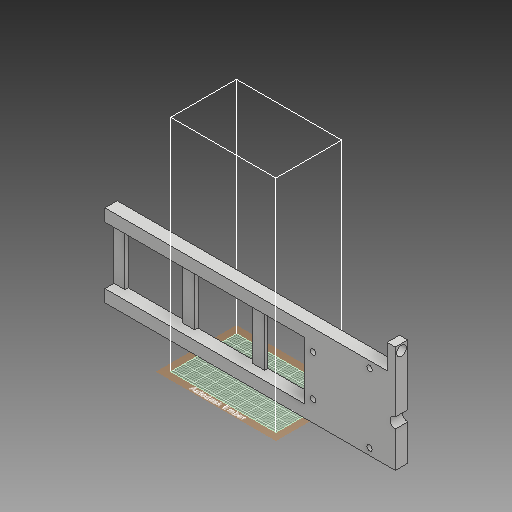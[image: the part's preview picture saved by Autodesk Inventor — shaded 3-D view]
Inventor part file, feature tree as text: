
AUTODESK INVENTOR PART (.ipt)
format: ipt  version: 2018 (Build 220112000, 112)  size: 1,129,472 bytes
history: native  units: mm
features: sketch x81, extrude x64, fillet x22, hole x8
ambient origin geometry x8: Origin, YZ Plane, XZ Plane, XY Plane, X Axis, Y Axis, Z Axis, Center Point
bodies: Solid1 (feature_tree)
feature tree (175):
  extrude  "Extrusion1"  Depth=50.0mm
  hole  "Hole1"  [1 undecoded]
  hole  "Hole2"  [1 undecoded]
  extrude  "Extrusion2"  Depth=25.0mm
  extrude  "Extrusion3"  Depth=25.0mm
  extrude  "Extrusion4"  Depth=5.0mm
  sketch  "Sketch7"  dims[d25=10.0mm d26=5.0mm]
  extrude  "Extrusion5"  Depth=5.0mm
  extrude  "Extrusion6"  Depth=35.0mm
  extrude  "Extrusion7"  Depth=35.0mm
  extrude  "Extrusion8"  Depth=35.0mm
  extrude  "Extrusion9"  Depth=2.0mm TaperAngle=0.0deg
  extrude  "Extrusion10"  Depth=7.5mm TaperAngle=0.0deg
  extrude  "Extrusion11"  Depth=10.0mm
  extrude  "Extrusion12"  Depth=7.5mm
  fillet  "Fillet1"  Radius=7.5mm
  fillet  "Fillet2"  Radius=25.0mm
  fillet  "Fillet3"  Radius=3.0mm
  fillet  "Fillet4"  Radius=3.2mm
  fillet  "Fillet5"  Radius=2.1mm
  fillet  "Fillet6"  Radius=5.5mm
  extrude  "Extrusion13"  Depth=92.5mm TaperAngle=0.0deg
  sketch  "Sketch17"  dims[d58=4.25mm d59=241.0mm d60=0.0mm]
  hole  "Hole3"  [1 undecoded]
  hole  "Hole4"  [1 undecoded]
  extrude  "Extrusion14"  Depth=5.0mm
  extrude  "Extrusion15"  Depth=2.5mm TaperAngle=0.0deg
  extrude  "Extrusion16"  Depth=6.35mm
  extrude  "Extrusion17"  Depth=2.5mm
  extrude  "Extrusion18"  Depth=14.55mm TaperAngle=0.0deg
  extrude  "Extrusion19"  Depth=0.1mm
  extrude  "Extrusion20"  Depth=3.25mm
  extrude  "Extrusion21"  Depth=3.25mm
  hole  "Hole5"  [1 undecoded]
  extrude  "Extrusion22"  Depth=2.0mm
  extrude  "Extrusion23"  Depth=15.0mm
  extrude  "Extrusion24"  Depth=10.0mm TaperAngle=0.0deg
  hole  "Hole6"  [1 undecoded]
  extrude  "Extrusion25"  Depth=100.0mm TaperAngle=0.0deg
  extrude  "Extrusion26"  Depth=2.0mm TaperAngle=0.0deg
  extrude  "Extrusion27"  Depth=3.3mm
  extrude  "Extrusion28"  Depth=3.3mm
  hole  "Hole7"  [1 undecoded]
  extrude  "Extrusion29"  Depth=8.0mm
  extrude  "Extrusion30"  Depth=17.0mm
  hole  "Hole8"  [1 undecoded]
  extrude  "Extrusion31"  Depth=3.5mm
  extrude  "Extrusion32"  Depth=10.0mm
  fillet  "Fillet7"  Radius=3.3mm
  fillet  "Fillet8"  Radius=10.0mm
  extrude  "Extrusion33"  Depth=5.0mm
  extrude  "Extrusion34"  Depth=5.0mm
  sketch  "Sketch45"  dims[d149=10.0mm d150=17.5mm d151=0.0mm]
  sketch  "Sketch46"  dims[d152=5.0mm]
  extrude  "Extrusion35"  Depth=10.0mm TaperAngle=0.0deg
  extrude  "Extrusion36"  Depth=8.0mm TaperAngle=0.0deg
  extrude  "Extrusion37"  Depth=3.75mm
  extrude  "Extrusion38"  Depth=3.75mm
  extrude  "Extrusion39"  Depth=10.0mm TaperAngle=0.0deg
  extrude  "Extrusion40"  Depth=2.0mm TaperAngle=0.0deg
  fillet  "Fillet9"  Radius=5.0mm
  fillet  "Fillet10"  Radius=15.0mm
  fillet  "Fillet11"  Radius=7.5mm
  fillet  "Fillet12"  Radius=17.5mm
  extrude  "Extrusion41"  Depth=47.5mm
  extrude  "Extrusion42"  Depth=5.0mm
  sketch  "Sketch55"  dims[d200=20.0mm d203=5.0mm]
  extrude  "Extrusion43"  Depth=5.0mm
  extrude  "Extrusion44"  Depth=7.5mm TaperAngle=0.0deg
  extrude  "Extrusion45"  Depth=4.0mm
  extrude  "Extrusion46"  Depth=12.0mm
  extrude  "Extrusion47"  Depth=7.5mm
  extrude  "Extrusion48"  Depth=20.0mm TaperAngle=0.0deg
  extrude  "Extrusion49"  Depth=20.0mm
  extrude  "Extrusion50"  Depth=4.0mm
  extrude  "Extrusion51"  Depth=10.0mm TaperAngle=0.0deg
  extrude  "Extrusion52"  Depth=5.5mm TaperAngle=0.0deg
  fillet  "Fillet13"  Radius=10.0mm
  fillet  "Fillet14"  Radius=74.724mm
  fillet  "Fillet15"  Radius=74.724mm
  fillet  "Fillet16"  Radius=85.515mm
  extrude  "Extrusion53"  Depth=5.0mm
  extrude  "Extrusion54"  Depth=5.0mm
  fillet  "Fillet17"  Radius=85.515mm
  extrude  "Extrusion55"  Depth=2.0mm TaperAngle=0.0deg
  fillet  "Fillet18"  Radius=2.0mm
  extrude  "Extrusion56"  Depth=2.0mm
  sketch  "Sketch70"  dims[d247=2.0mm d248=10.0mm d249=2.0mm d250=0.0mm d251=1.0mm d252=0.0mm]
  extrude  "Extrusion57"  Depth=10.0mm
  fillet  "Fillet19"  Radius=2.0mm
  fillet  "Fillet20"  Radius=1.0mm
  extrude  "Extrusion58"  Depth=1.0mm TaperAngle=0.0deg
  extrude  "Extrusion59"  Depth=0.349066mm
  fillet  "Fillet21"  Radius=0.349066mm
  sketch  "Sketch74"  dims[d262=4.0mm d263=10.0mm d264=0.0mm]
  extrude  "Extrusion60"  Depth=4.0mm
  sketch  "Sketch76"  dims[d270=3.0mm d271=24.5mm]
  extrude  "Extrusion61"  Depth=10.0mm TaperAngle=0.0deg
  extrude  "Extrusion62"  Depth=6.5mm
  fillet  "Fillet22"  Radius=5.5mm
  sketch  "Sketch79"  dims[d277=7.5mm d278=0.0mm]
  extrude  "Extrusion63"  Depth=24.5mm
  extrude  "Extrusion64"  Depth=5500.0mm TaperAngle=0.0deg
  sketch  "Sketch1"  dims[d0=50.0mm d1=50.0mm]
  sketch  "Sketch2"  dims[d2=240.0mm d3=7.5mm]
  sketch  "Sketch3"  dims[d4=7.5mm d5=7.5mm d6=0.0mm]
  sketch  "Sketch4"  dims[d7=6.35mm d8=6.0mm d9=4.0mm d10=2.0mm d11=90.0deg d12=8.0mm d13=20.594885mm d14=25.0mm]
  sketch  "Sketch5"  dims[d15=3.3mm d16=6.0mm d17=4.0mm d18=2.0mm d19=90.0deg d20=8.0mm d21=20.594885mm d22=25.0mm]
  sketch  "Sketch6"  dims[d23=180.0deg d24=5.0mm]
  sketch  "Sketch8"  dims[d27=17.5mm d28=0.0mm d30=35.0mm]
  sketch  "Sketch9"  dims[d31=35.0mm d32=35.0mm]
  sketch  "Sketch10"  dims[d33=35.0mm d34=35.0mm]
  sketch  "Sketch11"  dims[d35=35.0mm d36=2.0mm d37=0.0mm]
  sketch  "Sketch12"  dims[d38=10.0mm d39=7.5mm d40=0.0mm]
  sketch  "Sketch13"  dims[d41=100.0mm d42=10.0mm]
  sketch  "Sketch14"  dims[d43=7.5mm d44=0.0mm d45=7.5mm d46=7.5mm d47=25.0mm d48=0.0mm d49=3.0mm d50=3.2mm d51=2.1mm d52=5.5mm]
  sketch  "Sketch15"  dims[d53=3.3mm d54=92.5mm d55=0.0mm]
  sketch  "Sketch16"  dims[d56=5.5mm d57=3.3mm]
  sketch  "Sketch18"  dims[d61=4.44mm d62=5.0mm]
  sketch  "Sketch19"  dims[d63=2.5mm d64=91.25mm d65=0.0mm]
  sketch  "Sketch20"  dims[d66=30.0mm d67=6.35mm]
  sketch  "Sketch21"  dims[d68=3.8mm d69=0.0mm d70=2.5mm]
  sketch  "Sketch22"  dims[d71=14.55mm d72=0.0mm d73=14.55mm d74=0.0mm]
  sketch  "Sketch23"  dims[d75=0.1mm d76=0.1mm]
  sketch  "Sketch24"  dims[d77=3.25mm d78=3.25mm]
  sketch  "Sketch25"  dims[d79=3.25mm d80=3.25mm]
  sketch  "Sketch26"  dims[d81=35.0mm d82=10.0mm]
  sketch  "Sketch27"  dims[d83=2.0mm d84=0.0mm d85=3.6mm]
  sketch  "Sketch28"  dims[d86=3.6mm]
  sketch  "Sketch29"  dims[d87=3.3mm d88=6.0mm d89=4.0mm d90=2.0mm d91=90.0deg d92=15.0mm d93=20.594885mm]
  sketch  "Sketch30"  dims[d94=3.3mm d95=6.0mm d96=4.0mm d97=2.0mm d98=90.0deg d99=15.0mm d100=20.594885mm d101=6.0mm]
  sketch  "Sketch31"  dims[d102=20.0mm d103=0.0mm d104=10.0mm d105=0.0mm]
  sketch  "Sketch32"  dims[d106=2.0mm d107=0.0mm d108=4.0mm]
  sketch  "Sketch33"  dims[d109=100.0mm d110=0.0mm d111=100.0mm d112=0.0mm]
  sketch  "Sketch34"  dims[d113=5.0mm d114=2.0mm d115=0.0mm]
  sketch  "Sketch35"  dims[d116=3.3mm d117=3.3mm]
  sketch  "Sketch36"  dims[d118=3.3mm d119=3.3mm]
  sketch  "Sketch37"  dims[d120=2.0mm d121=0.0mm d122=5.5mm d123=0.0mm]
  sketch  "Sketch38"  dims[d124=3.3mm d125=6.0mm d126=4.0mm d127=2.0mm d128=90.0deg d129=8.0mm d130=20.594885mm d131=42.0mm]
  sketch  "Sketch39"  dims[d132=17.0mm d133=21.0mm]
  sketch  "Sketch40"  dims[d135=8.5mm d136=15.825mm]
  sketch  "Sketch41"  dims[d137=3.5mm d138=21.0mm]
  sketch  "Sketch42"  dims[d139=3.3mm d140=3.3mm d141=3.3mm d142=10.0mm d143=0.0mm]
  sketch  "Sketch43"  dims[d144=7.5mm d145=0.0mm d146=5.0mm]
  sketch  "Sketch44"  dims[d147=10.0mm d148=5.0mm]
  sketch  "Sketch47"  dims[d153=7.0mm d154=6.0mm d155=4.0mm d156=2.0mm d157=90.0deg d158=8.0mm d159=20.594885mm d160=17.5mm d161=0.0mm]
  sketch  "Sketch48"  dims[d162=170.5mm d163=0.0mm d164=3.75mm]
  sketch  "Sketch49"  dims[d165=3.75mm d166=3.75mm]
  sketch  "Sketch50"  dims[d167=3.75mm d168=10.0mm d169=0.0mm]
  sketch  "Sketch51"  dims[d170=100.0mm d171=0.0mm]
  sketch  "Sketch52"  dims[d172=5.0mm d173=6.0mm d174=4.0mm d175=2.0mm d176=90.0deg d177=15.0mm d178=0.0mm d179=2.0mm d180=0.0mm d181=5.0mm d182=15.0mm d183=0.0mm d184=7.5mm]
  sketch  "Sketch53"  dims[d185=6.0mm d186=6.0mm d187=4.0mm d188=2.0mm d189=90.0deg d190=15.0mm d191=0.0mm d192=17.5mm d193=0.0mm]
  sketch  "Sketch54"  dims[d194=23.75mm d195=47.5mm]
  sketch  "Sketch56"  dims[d204=5.0mm d205=29.0mm]
  sketch  "Sketch57"  dims[d206=29.0mm d207=7.5mm d208=0.0mm]
  sketch  "Sketch58"  dims[d209=4.0mm d210=4.0mm]
  sketch  "Sketch59"  dims[d211=2.0mm d212=0.0mm d213=12.0mm]
  sketch  "Sketch60"  dims[d214=2.0mm d215=0.0mm d216=7.5mm]
  sketch  "Sketch61"  dims[d217=7.5mm d218=20.0mm d219=0.0mm]
  sketch  "Sketch62"  dims[d220=20.0mm d221=3.3mm]
  sketch  "Sketch63"  dims[d222=20.0mm d223=0.0mm d224=4.0mm]
  sketch  "Sketch64"  dims[d225=4.0mm d226=10.0mm d227=0.0mm]
  sketch  "Sketch65"  dims[d228=3.0mm d229=5.5mm d230=0.0mm d231=10.0mm d232=0.0mm d233=74.724mm d234=74.724mm d235=85.515mm]
  sketch  "Sketch66"  dims[d236=5.0mm d237=5.0mm]
  sketch  "Sketch67"  dims[d238=85.515mm d239=5.0mm d240=85.515mm]
  sketch  "Sketch68"  dims[d241=5.0mm d242=2.0mm d243=0.0mm d244=2.0mm]
  sketch  "Sketch69"  dims[d245=2.0mm d246=2.0mm]
  sketch  "Sketch71"  dims[d253=20.0mm d254=1.0mm d255=0.0mm]
  sketch  "Sketch72"  dims[d256=0.5mm d257=0.0mm d258=0.349066mm d259=0.349066mm]
  sketch  "Sketch73"  dims[d260=4.0mm d261=4.0mm]
  sketch  "Sketch75"  dims[d265=5.5mm d266=0.0mm d267=6.5mm d268=5.5mm d269=0.0mm]
  sketch  "Sketch77"  dims[d272=5500.0mm d273=0.0mm d274=5500.0mm d275=0.0mm]
  sketch  "Sketch78"  dims[d276=24.5mm]
  sketch  "Sketch80"  dims[d279=7.5mm d280=0.0mm]
  sketch  "Sketch81"  dims[d281=7.5mm d282=0.0mm d283=2.0mm d284=2.0mm d285=4.0mm d286=1.5mm d287=4.25mm d288=4.25mm d289=7.5mm d290=0.0mm d291=20.025mm d292=10.0mm d293=2.5mm d294=17.0mm d295=0.0mm d296=1.5mm d298=3.0mm d300=3.0mm d301=5.0mm d302=0.0mm d303=1.0mm d304=10.0mm d305=0.0mm d306=8.45mm d307=8.45mm d308=5.5mm d309=9.5mm d310=17.0mm d311=0.0mm d312=2.0mm d313=2.0mm d314=5.5mm d315=0.0mm d316=9.5mm d317=0.0mm d318=2.0mm d321=4.5mm d322=17.0mm d323=0.0mm d324=11.5mm d325=2.88mm d326=2.88mm d327=3.0mm d328=3.0mm d329=2.5mm d330=0.0mm d331=3.0mm d332=2.5mm d333=0.0mm d334=1.0mm d335=11.0mm d336=4.75mm d337=2.0mm d338=0.0mm d339=6.0mm d340=5.5mm d341=0.0mm]
note: 8 required parameter values undecoded (feature->parameter linkage not recoverable at this tier; creation-order binding heuristic only, values carry confidence <= 0.55)
